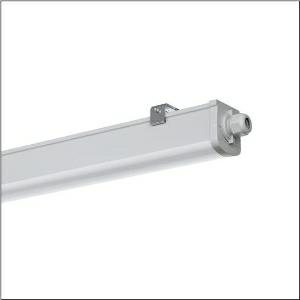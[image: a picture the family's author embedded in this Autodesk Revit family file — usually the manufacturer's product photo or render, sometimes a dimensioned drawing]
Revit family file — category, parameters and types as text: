
# Revit family: monsun_r__31_51fa20dd420b_de40
name_source: partatom
category: Lighting Fixtures
units: mm (PartAtom-declared; Revit-internal decimal feet)

## family parameters
Cut with Voids When Loaded = No
Host = Face
Light Source = No
Part Type = Normal
Room Calculation Point = No
Round Connector Dimension = Use Diameter
Shared = No

## types (1)
- Monsun® 31 (1 x LED, 2300 lm, 19 W, 4000K)
    Apparent Load = 19 VA
    CIE Flux Codes = 42 72 91 92 100
    Color Rendering = 80
    Color Temperature = 4000K
    Default Elevation = 1800 mm
    Description = Monsun® 31, damp-proof luminaire, primary optical cover: diffuser, of PC, frosted, light emission: direct distribution, primary light characteristic: symmetric, installation type: surface-mounted, LED, rated luminous flux: 2.300lm, luminous efficacy: 121lm/W, light colour: 840, colour temperature: 4000K, control gear: DALI 2, with terminal, 5+1-pole, max. 2.5mm², through-wiring: 3x 2.5mm² + 3x 1.5mm², mains connection: 220..240V, AC, 50/60Hz, rated input power: 19W, housing, luminaire housing, of PC, light grey (RAL 7035), length: 558mm, width: 68mm, height: 76mm, protection rating (complete): IP66, insulation class (complete): insulation class II (safety insulation), certification: CE, ENEC, UKCA, protection symbol: D, impact resistance: IK08, permissible operating ambient temperature: -20..+40°C, corresponds to IFS (International Featured Standards) requirements for safety and quality in the food industry, contact your sales advisor before using the luminaires in applications with unclear chemical exposure, large temperature fluctuations or condensation-forming humidity, packaging unit: 1 piece
    Height = 77 mm
    Lamp = 1 x LED
    Lamp Light Flux = 2300 lm
    Lamp Power = 19 W
    Lamp count = 1
    Length = 618 mm
    Luminous efficacy = 121 lm/W
    Manufacturer = Siteco
    ModVariant = No
    Model = 51FA20DD420B
    Mounting Place = Ceiling
    Mounting Type = Surface mounted
    Number of Poles = 1
    OnlyDefault = Yes
    Power Factor = 1
    Product Name = Monsun® 31
    Product group = damp-proof luminaire
    ProductGroupID = 300
    Protection Class = Protection class II
    Protection Degree = IP 66
    RLX_Detail_Level = 1
    RLX_Emergency_Light_Flux = 0 lm
    RLX_Emergency_Type = 0
    RLX_Emergency_Type_DB = No
    RlxData = <blob elided: 32861 chars, md5=8eec10b0>
    Socket = socket
    Standby Power = 0 W
    System Light Flux = 2300 lm
    System Power = 19 W
    Type Comments = Product without accessories
    Type Image = l_1006174.jpg
    URL = http://relux.com
    VarID = ---
    Voltage = 0 V
    Weight = 0.00 kg
    Width = 69 mm

## geometry (parser evidence)
native form markers: Blend x4, Sweep x14
no freeform markers — native parametric forms only
